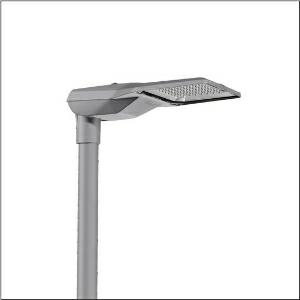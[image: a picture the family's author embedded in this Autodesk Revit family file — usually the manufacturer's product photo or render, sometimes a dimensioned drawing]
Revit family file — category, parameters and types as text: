
# Revit family: streetlight_sl_21_midi___st1_0a_5xe3d33s08mb_8b67
name_source: partatom
category: Lighting Fixtures
units: mm (PartAtom-declared; Revit-internal decimal feet)

## family parameters
Cut with Voids When Loaded = No
Host = Face
Light Source = No
Part Type = Normal
Room Calculation Point = No
Round Connector Dimension = Use Diameter
Shared = No

## types (1)
- --- (1 x LED, 18270 lm, 136 W, 3000K)
    Apparent Load = 136 VA
    CIE Flux Codes = 37 72 97 100 100
    Color Rendering = 70
    Color Temperature = 3000K
    Default Elevation = 1800 mm
    Description = Streetlight SL 21 midi, mast luminaire, primary light control with lens, of PMMA, primary optical cover: cover, of toughened safety glass, transparent, light distribution: ST1.0a, light emission: direct distribution, primary light characteristic: asymmetric, installation type: side-entry, post-top, LED, High Power LED, rated luminous flux: 18.270lm, luminous efficacy: 134lm/W, light colour: 730, colour temperature: 3000K, control gear: D4i, control: flexible luminous flux parameterisation, time-dependent luminous flux control, constant luminous flux control, overheat protection, pre-setting: logarithmic dimming characteristic, mains connection: 230..240V, AC, 50/60Hz, start of lifetime: 136W, end of service life: 142W, reduction: 61W, luminaire housing, of diecast aluminium, powder-coated, Siteco® metallic grey (DB 702S), corrosivity category C5 mid according to DIN EN ISO 12944, please order mast flange separately, inclination adjustable: 0°, 5°, 10°, 15°, sealing non-destructively replaceable, multi-level sealing system, length: 644mm, width: 335mm, height: 110mm, mast flange for spigot size: 42mm (side-entry): 5XC10008XM4, 60/48mm (side-entry/post-top): 5XC10108XM2, 76/60mm (side-entry/post-top): 5XC10108XM1, mounting height: 4..8m, Smart Interface above, protection rating (complete): IP66, insulation class (complete): insulation class II (safety insulation), certification: CE, ENEC, ENEC+, VDE, impact resistance: IK10, permissible operating ambient temperature for outdoor applications: -40..+50°C, standard-compliant lighting for roads and squares, packaging unit: 1 piece

Light Distribution: ST1.0a
    Height = 111 mm
    Lamp = 1 x LED
    Lamp Light Flux = 18270 lm
    Lamp Power = 136 W
    Lamp count = 1
    Length = 644 mm
    Luminous efficacy = 134 lm/W
    Manufacturer = Siteco
    ModVariant = No
    Model = 5XE3D33S08MB
    Number of Poles = 1
    OnlyDefault = Yes
    Power Factor = 1
    Product Name = Streetlight SL 21 midi | ST1.0a
    Product group = mast luminaire | pylon top
    ProductGroupID = 6100
    Protection Class = Protection class II
    Protection Degree = IP 66
    RLX_Detail_Level = 1
    RLX_Emergency_Light_Flux = 0 lm
    RLX_Emergency_Type = 0
    RLX_Emergency_Type_DB = No
    RlxData = <blob elided: 26837 chars, md5=c18e9b32>
    Socket = socket
    Standby Power = 0 W
    System Light Flux = 18270 lm
    System Power = 136 W
    Type Comments = factory setting: luminous flux: 100 % | dim-lin: 254 | 695 mA
    Type Image = l_1004302.jpg
    URL = http://relux.com
    VarID = @adj_210643
    Voltage = 0 V
    Weight = 0.00 kg
    Width = 336 mm

## geometry (parser evidence)
native form markers: Blend x4, Sweep x12
no freeform markers — native parametric forms only
